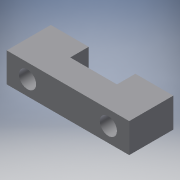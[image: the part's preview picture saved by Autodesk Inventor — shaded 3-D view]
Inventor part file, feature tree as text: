
AUTODESK INVENTOR PART (.ipt)
format: ipt  version: 2017 SP1 (Build 210196100, 196)  size: 122,368 bytes
history: native  units: mm
features: extrude x4, sketch x4, projected_geometry x1
ambient origin geometry x8: Origin, YZ Plane, XZ Plane, XY Plane, X Axis, Y Axis, Z Axis, Center Point
bodies: Solid1 (feature_tree)
feature tree (9):
  extrude  "Extrusion1"  Depth=10.0mm
  extrude  "Extrusion2"  Depth=6.0mm TaperAngle=0.0deg
  extrude  "Extrusion3"  Depth=6.0mm TaperAngle=0.0deg
  extrude  "Extrusion4"  Depth=10.0mm TaperAngle=0.0deg
  sketch  "Sketch1"  dims[d0=4.0mm d1=10.0mm]
  sketch  "Sketch2"  dims[d2=25.0mm d3=6.0mm d4=0.0mm]
  projected_geometry  "Projected Loop1"
  sketch  "Sketch3"  dims[d5=3.5mm d6=6.0mm d7=0.0mm]
  sketch  "Sketch4"  dims[d8=1.0mm d9=10.0mm d10=0.0mm d11=9.525mm d12=10.0mm d13=0.0mm]
